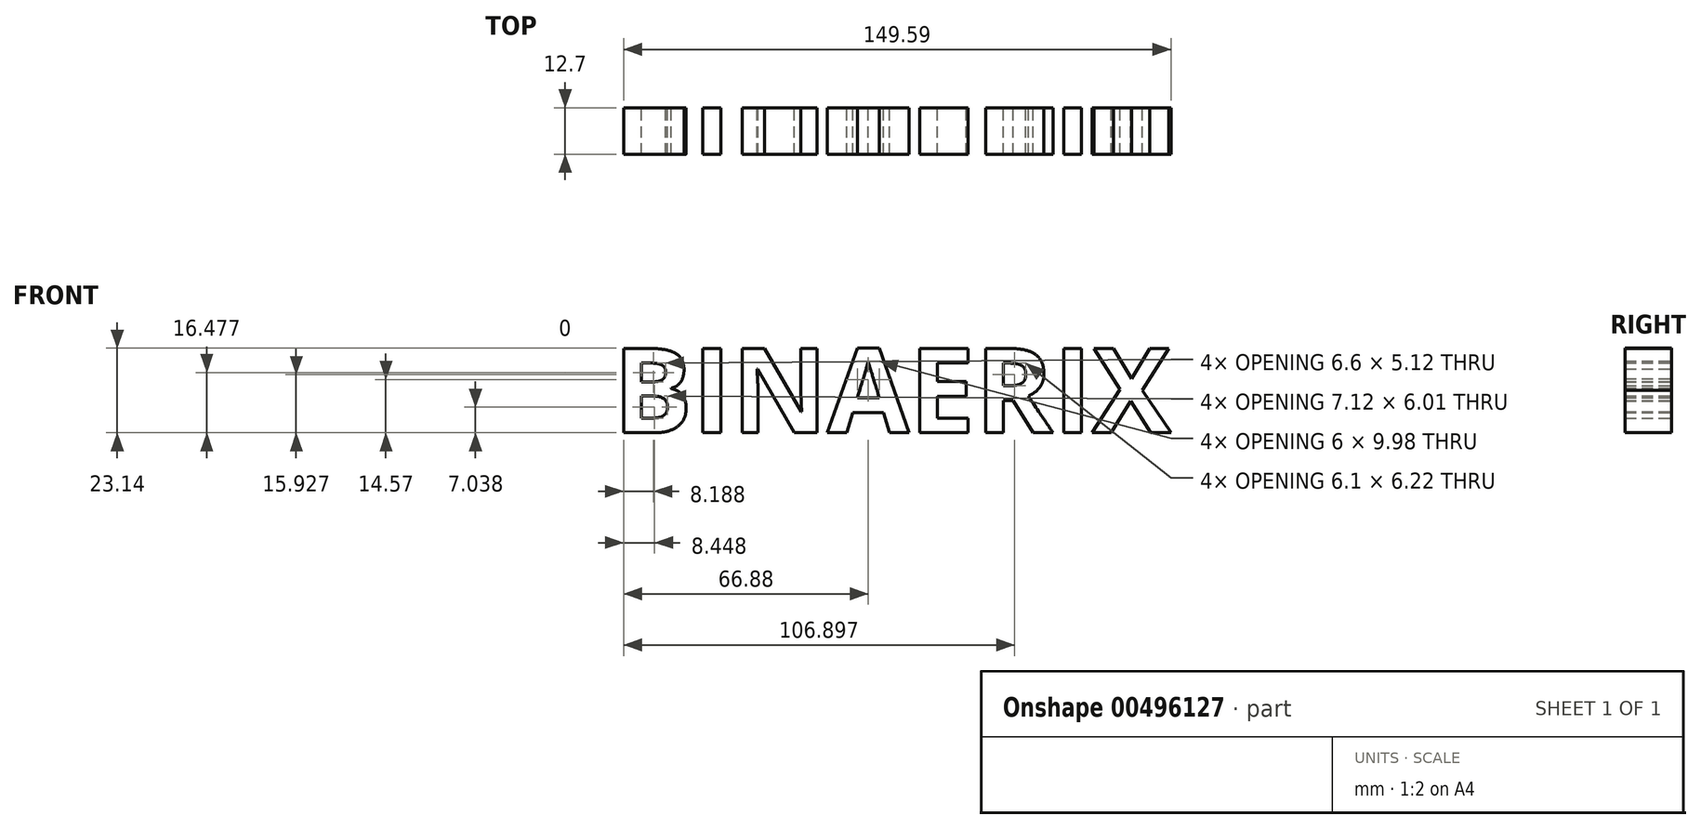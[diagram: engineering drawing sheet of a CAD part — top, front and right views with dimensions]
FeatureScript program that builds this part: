
annotation { "Feature Type Name" : "Feature", "Feature Type Description" : "" }
export const myFeature = defineFeature(function(context is Context, id is Id, definition is map)
    precondition{}
    {
        {
            var Q0;
            Q0=qCreatedBy(makeId("Front.planeOp"),FACE);
            var sketch = newSketch(context, id + "F0", { "sketchPlane" : qUnion([Q0])});
            skText(sketch, "E0", { "text": "BINAERIX", "fontName": "OpenSans-Bold.ttf"});
            const initialGuessF0  = {"E0": [-0.08085, -0.01496, 1, 0, 0.02324]};
            skSetInitialGuess(sketch, initialGuessF0);
            skSolve(sketch);
        }
        {
            var Q0;
            Q0 = qSketchRegion(id + "F0", true);
            extrude(context, id + "F1", {"entities" : qUnion([Q0]), "depth" : 12.7 * mm});
        }
    });
